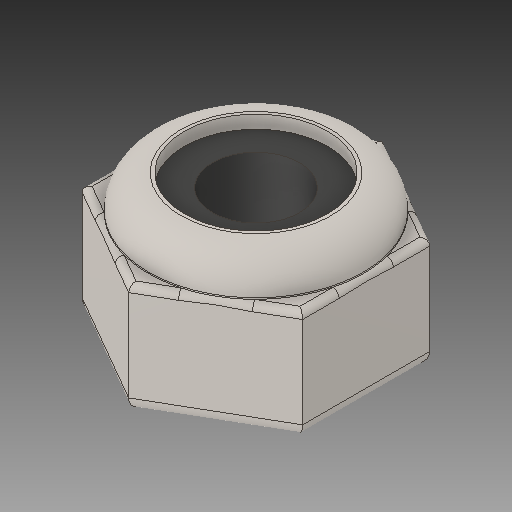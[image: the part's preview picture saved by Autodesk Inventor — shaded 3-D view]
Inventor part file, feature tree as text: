
AUTODESK INVENTOR PART (.ipt)
format: ipt  version: 2017 (Build 210142000, 142)  size: 202,752 bytes
history: native  units: in
note: dims shown in document units (in); Inventor stores cm internally (conversion verified against a paired STEP export)
features: fillet x1
ambient origin geometry x8: Origin, YZ Plane, XZ Plane, XY Plane, X Axis, Y Axis, Z Axis, Center Point
bodies: Solid1 (feature_tree)
feature tree (1):
  fillet  "Fillet6"  [1 undecoded]
note: 1 required parameter value undecoded (feature->parameter linkage not recoverable at this tier; creation-order binding heuristic only, values carry confidence <= 0.55)
